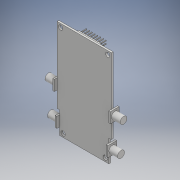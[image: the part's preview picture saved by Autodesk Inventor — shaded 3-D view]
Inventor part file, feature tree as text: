
AUTODESK INVENTOR PART (.ipt)
format: ipt  version: 2018 (Build 220112000, 112)  size: 298,496 bytes
history: native  units: mm
features: extrude x9, sketch x9, mirror x1
ambient origin geometry x8: Origin, YZ Plane, XZ Plane, XY Plane, X Axis, Y Axis, Z Axis, Center Point
bodies: Solid1 (feature_tree)
feature tree (19):
  extrude  "Extrusion1"  Depth=45.0mm
  extrude  "Extrusion2"  Depth=68.7mm
  extrude  "Extrusion3"  Depth=1.63mm TaperAngle=0.0deg
  extrude  "Extrusion4"  Depth=4.0mm
  sketch  "Sketch5"  dims[d9=3.25mm d10=3.25mm]
  extrude  "Extrusion5"  Depth=3.25mm
  extrude  "Extrusion6"  Depth=3.25mm
  mirror  "Mirror1"
  extrude  "Extrusion7"  Depth=3.25mm
  extrude  "Extrusion8"  Depth=1.63mm TaperAngle=0.0deg
  extrude  "Extrusion9"  Depth=8.0mm
  sketch  "Sketch1"  dims[d0=49.6mm d1=45.0mm]
  sketch  "Sketch2"  dims[d2=89.0mm d3=68.7mm]
  sketch  "Sketch3"  dims[d4=50.0mm d5=1.63mm d6=0.0mm]
  sketch  "Sketch4"  dims[d7=4.0mm d8=3.25mm]
  sketch  "Sketch6"  dims[d11=3.25mm d12=3.25mm]
  sketch  "Sketch7"  dims[d13=3.25mm d14=3.25mm]
  sketch  "Sketch8"  dims[d15=3.25mm d16=1.63mm d17=0.0mm]
  sketch  "Sketch9"  dims[d18=9.6mm d19=8.0mm d20=49.5mm d21=1.5mm d22=0.0mm d23=9.6mm d24=8.0mm d25=11.5mm d26=1.5mm d27=0.0mm d28=6.3mm d29=6.3mm d30=8.0mm d31=0.0mm d32=8.0mm d33=0.0mm d34=20.58mm d35=5.08mm d36=1.25mm d38=15.6mm d39=2.4mm d40=0.0mm d41=0.64mm d42=1.65mm d43=1.65mm d44=80.0mm d46=2.54mm d47=20.0mm d49=2.54mm d52=5.76mm d53=0.0mm d54=5.08mm d55=2.54mm d56=16.6mm d57=24.2mm d58=11.3mm d59=0.0mm]
